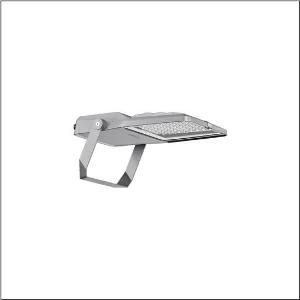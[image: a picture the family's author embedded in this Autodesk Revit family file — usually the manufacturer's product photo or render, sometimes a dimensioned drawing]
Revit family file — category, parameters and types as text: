
# Revit family: floodlight_fl_21_iq_mini___pl64_5xa7772d4e1a_07d3
name_source: partatom
category: Lighting Fixtures
units: mm (PartAtom-declared; Revit-internal decimal feet)

## family parameters
Cut with Voids When Loaded = No
Host = Face
Light Source = No
Part Type = Normal
Room Calculation Point = No
Round Connector Dimension = Use Diameter
Shared = No

## types (1)
- --- (1 x LED, 17970 lm, 143 W, 4000K)
    Apparent Load = 143 VA
    CIE Flux Codes = 28 80 98 100 100
    Color Rendering = 70
    Color Temperature = 4000K
    Default Elevation = 1800 mm
    Description = Floodlight FL 21 iQ mini, floodlight, primary light control with lens, of PMMA, primary optical cover: protective disc, of toughened safety glass, transparent, light distribution: PL64, light emission: direct distribution, installation type: surface-mounted, lamps: LED, High Power LED, rated values: 17.970lm | 143W | 125,7lm/W (begin service life); end service life: 17.970lm | 151,6W; at 50% lumin. flux: 8.985lm | 60,8W | 147,8lm/W, colour temperature: 4000K, colour rendering: CRI > 70, light colour: 740, light setting 1 begin service life: 100% | 17.970lm | 143W | 125,7lm/W | 4.000K, light setting 1 end service life: 151,6W, further light settings possible, control: Street-Remote, Auto-Match, Temp-Guard, Night-Set, Smart-Wire, Desk-Remote (wireless, voltage-free reading and setting of iQ features in the workshop via application-optimized NFC function/RFID function), optimised constant luminous flux control (CLO 2.0), pre-setting: linear dimming characteristic, with terminal, 6-pole, mains connection: 220..240V, AC, 50/60Hz, luminaire housing, of diecast aluminium, powder-coated, SITECO metallic grey (DB 702S), corrosivity category C5 mid according to DIN EN ISO 12944suitable for swimming poolschlorine-resistant, sealing non-destructively replaceable, mounting bracket, of steel, galvanised, powder-coated, SITECO metallic grey (DB 702S), protection rating (complete): IP66, insulation class (complete): insulation class II (safety insulation), certification: CE, ENEC, VDE, protection symbol: D, impact resistance: IK08, permissible operating ambient temperature: -40..+40°C, permissible operating ambient temperature for outdoor applications: -40..+50°C, standard: DIN EN 12944, LABS conformity tested according to VDMA 24364:2018-05, packaging unit: 1 piece

Light Distribution: PL64
    Height = 70 mm
    Lamp = 1 x LED
    Lamp Light Flux = 17970 lm
    Lamp Power = 143 W
    Lamp count = 1
    Length = 485 mm
    Luminous efficacy = 126 lm/W
    Manufacturer = Siteco
    ModVariant = No
    Model = 5XA7772D4E1A
    Mounting Place = Pole
    Mounting Type = Pole annexe
    Number of Poles = 1
    OnlyDefault = Yes
    Power Factor = 1
    Product Name = Floodlight FL 21 iQ mini | PL64
    Product group = floodlight | pylon annexe
    ProductGroupID = 6201
    Protection Class = Protection class II
    Protection Degree = IP 66
    RLX_Detail_Level = 1
    RLX_Emergency_Light_Flux = 0 lm
    RLX_Emergency_Type = 0
    RLX_Emergency_Type_DB = No
    RlxData = <blob elided: 96805 chars, md5=215deb8a>
    Socket = socket
    Standby Power = 0 W
    System Light Flux = 17970 lm
    System Power = 143 W
    Type Comments = factory setting: luminous flux: 100 % | dim-lin: 254 | 730 mA
    Type Image = l_1006845.jpg
    URL = http://relux.com
    VarID = @adj_166759
    Voltage = 0 V
    Weight = 0.00 kg
    Width = 337 mm

## geometry (parser evidence)
native form markers: Blend x4, Sweep x13
no freeform markers — native parametric forms only
